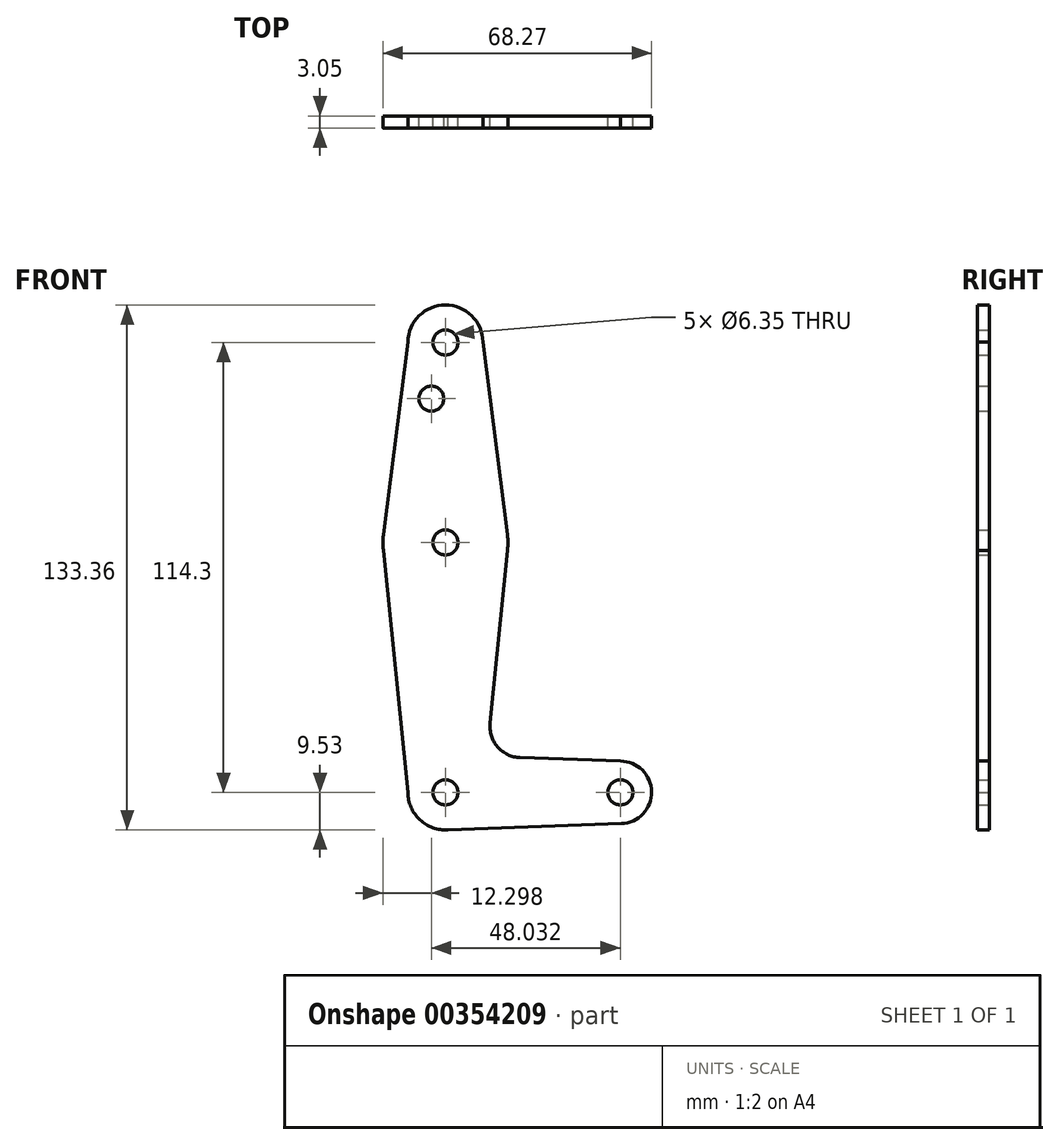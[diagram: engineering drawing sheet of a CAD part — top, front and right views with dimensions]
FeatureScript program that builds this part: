
annotation { "Feature Type Name" : "Feature", "Feature Type Description" : "" }
export const myFeature = defineFeature(function(context is Context, id is Id, definition is map)
    precondition{}
    {
        {
            var Q0;
            Q0=qCreatedBy(makeId("Front.planeOp"),FACE);
            var sketch = newSketch(context, id + "F0", { "sketchPlane" : qUnion([Q0])});
            skLineSegment(sketch, "E0", {"start": v(0, 0) * mm, "end": v(0, 114.3) * mm, "construction": true});
            skLineSegment(sketch, "E1", {"start": v(0, 0) * mm, "end": v(44.45, 0) * mm, "construction": true});
            skCircle(sketch, "E2", {"center": v(0, 114.3) * mm, "radius": 9.53 * mm});
            skCircle(sketch, "E3", {"center": v(0, 63.5) * mm, "radius": 15.88 * mm});
            skCircle(sketch, "E4", {"center": v(0, 0) * mm, "radius": 9.53 * mm});
            skCircle(sketch, "E5", {"center": v(44.45, 0) * mm, "radius": 7.94 * mm});
            skLineSegment(sketch, "E6", {"start": v(-9.26, 116.51) * mm, "end": v(-15.75, 65.5) * mm});
            skLineSegment(sketch, "E7", {"start": v(9.26, 116.51) * mm, "end": v(15.75, 65.5) * mm});
            skLineSegment(sketch, "E8", {"start": v(-15.75, 61.5) * mm, "end": v(-9.53, 0) * mm});
            skLineSegment(sketch, "E9", {"start": v(15.75, 61.5) * mm, "end": v(11.34, 17.59) * mm});
            skLineSegment(sketch, "E10", {"start": v(18.97, 8.85) * mm, "end": v(44.45, 7.94) * mm});
            skLineSegment(sketch, "E11", {"start": v(0, -9.53) * mm, "end": v(44.73, -7.93) * mm});
            skCircle(sketch, "E12", {"center": v(0, 114.3) * mm, "radius": 3.18 * mm});
            skCircle(sketch, "E13", {"center": v(0, 63.5) * mm, "radius": 3.18 * mm});
            skCircle(sketch, "E14", {"center": v(0, 0) * mm, "radius": 3.18 * mm});
            skCircle(sketch, "E15", {"center": v(44.45, 0) * mm, "radius": 3.18 * mm});
            skCircle(sketch, "E16", {"center": v(-3.58, 100.03) * mm, "radius": 3.18 * mm});
            skPoint(sketch, "E17.newPointA", {"position": v(9.57, 0) * mm});
            skArc(sketch, "E17.filletArc", {"start": v(11.34, 17.59) * mm, "mid": v(13.26, 11.57) * mm, "end": v(18.97, 8.85) * mm});
            skSolve(sketch);
        }
        {
            var Q0;
            Q0 = qSketchRegion(id + "F0", true);
            var Q1;
            {var subQ0=sQuery(id+"F0.wireOp",EDGE,"E14");var subQ1=sQuery(id+"F0.wireOp",EDGE,"E0");var subQ2=makeQuery(id+"F0.imprint","INTERSECT",VERTEX,{"derivedFrom":[subQ1,subQ0]});Q1=makeQuery(id+"F0.imprint","IMPRINT",FACE,{"disambiguationData":[TD([[makeQuery(id+"F0.imprint","IMPRINT",EDGE,{"disambiguationData":[TD([[subQ2,-1.0]])],"derivedFrom":subQ1}),-1.0]])]});}
            extrude(context, id + "F1", {"entities" : qUnion([Q0, Q1]), "depth" : 3.05 * mm});
        }
    });
